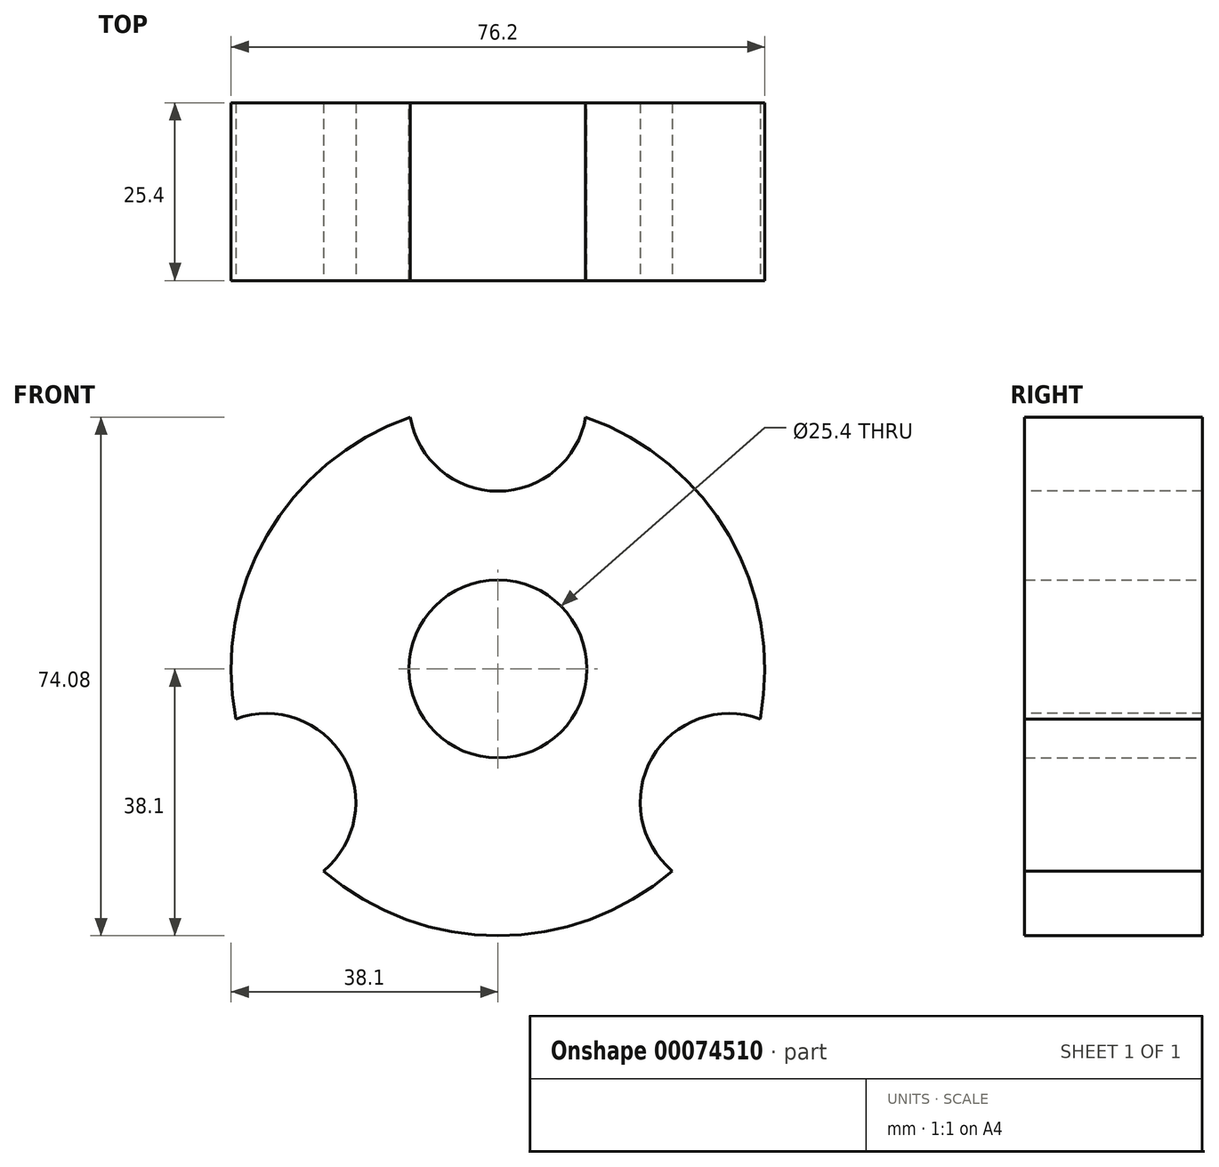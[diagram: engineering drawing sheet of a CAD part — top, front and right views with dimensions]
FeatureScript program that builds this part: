
annotation { "Feature Type Name" : "Feature", "Feature Type Description" : "" }
export const myFeature = defineFeature(function(context is Context, id is Id, definition is map)
    precondition{}
    {
        {
            var Q0;
            Q0=qCreatedBy(makeId("Front.planeOp"),FACE);
            var sketch = newSketch(context, id + "F0", { "sketchPlane" : qUnion([Q0])});
            skCircle(sketch, "E0", {"center": v(0, 0) * mm, "radius": 38.1 * mm});
            skCircle(sketch, "E1", {"center": v(0, 0) * mm, "radius": 12.7 * mm});
            skSolve(sketch);
        }
        {
            var Q0;
            Q0=makeQuery(id+"F0.imprint","IMPRINT",FACE,{"disambiguationData":[TD([[makeQuery(id+"F0.imprint","IMPRINT",EDGE,{"derivedFrom":sQuery(id+"F0.wireOp",EDGE,"E0")}),1.0]])]});
            extrude(context, id + "F1", {"entities" : qUnion([Q0]), "depth" : 25.4 * mm});
        }
        {
            var Q0;
            Q0=makeQuery(id+"F1.opExtrude","CAP_FACE",FACE,{"disambiguationData":[OSD([sQuery(id+"F0.wireOp",EDGE,"E0"),sQuery(id+"F0.wireOp",EDGE,"E1")])],"isStart":false});
            var sketch = newSketch(context, id + "F2", { "sketchPlane" : qUnion([Q0])});
            skCircle(sketch, "E2", {"center": v(0, 38.1) * mm, "radius": 12.7 * mm});
            skCircle(sketch, "E3.1.0", {"center": v(-33, -19.05) * mm, "radius": 12.7 * mm});
            skCircle(sketch, "E3.2.0", {"center": v(33, -19.05) * mm, "radius": 12.7 * mm});
            skPoint(sketch, "E3.center", {"position": v(0, 0) * mm});
            skSolve(sketch);
        }
        {
            var Q0;
            {var subQ0=sQuery(id+"F2.wireOp",EDGE,"E2");var subQ1=makeQuery(id+"F1.opExtrude","CAP_EDGE",EDGE,{"disambiguationData":[OSD([sQuery(id+"F0.wireOp",EDGE,"E0")])],"isStart":false});var subQ2=makeQuery(id+"F2.imprint","INTERSECT",VERTEX,{"disambiguationData":[OD(0.0)],"derivedFrom":[subQ1,subQ0]});Q0=makeQuery(id+"F2.imprint","IMPRINT",FACE,{"disambiguationData":[TD([[makeQuery(id+"F2.imprint","IMPRINT",EDGE,{"disambiguationData":[TD([[subQ2,1.0]])],"derivedFrom":subQ0}),1.0]])]});}
            var Q1;
            {var subQ0=sQuery(id+"F2.wireOp",EDGE,"E3.1.0");var subQ1=makeQuery(id+"F1.opExtrude","CAP_EDGE",EDGE,{"disambiguationData":[OSD([sQuery(id+"F0.wireOp",EDGE,"E0")])],"isStart":false});var subQ2=makeQuery(id+"F2.imprint","INTERSECT",VERTEX,{"disambiguationData":[OD(0.0)],"derivedFrom":[subQ1,subQ0]});Q1=makeQuery(id+"F2.imprint","IMPRINT",FACE,{"disambiguationData":[TD([[makeQuery(id+"F2.imprint","IMPRINT",EDGE,{"disambiguationData":[TD([[subQ2,-1.0]])],"derivedFrom":subQ0}),1.0]])]});}
            var Q2;
            {var subQ0=sQuery(id+"F2.wireOp",EDGE,"E3.2.0");var subQ1=makeQuery(id+"F1.opExtrude","CAP_EDGE",EDGE,{"disambiguationData":[OSD([sQuery(id+"F0.wireOp",EDGE,"E0")])],"isStart":false});var subQ2=makeQuery(id+"F2.imprint","INTERSECT",VERTEX,{"disambiguationData":[OD(0.0)],"derivedFrom":[subQ1,subQ0]});Q2=makeQuery(id+"F2.imprint","IMPRINT",FACE,{"disambiguationData":[TD([[makeQuery(id+"F2.imprint","IMPRINT",EDGE,{"disambiguationData":[TD([[subQ2,-1.0]])],"derivedFrom":subQ0}),1.0]])]});}
            var Q3;
            {var subQ0=sQuery(id+"F2.wireOp",EDGE,"E2");var subQ1=makeQuery(id+"F1.opExtrude","CAP_EDGE",EDGE,{"disambiguationData":[OSD([sQuery(id+"F0.wireOp",EDGE,"E0")])],"isStart":false});var subQ2=makeQuery(id+"F2.imprint","INTERSECT",VERTEX,{"disambiguationData":[OD(0.0)],"derivedFrom":[subQ1,subQ0]});Q3=makeQuery(id+"F2.imprint","IMPRINT",FACE,{"disambiguationData":[TD([[makeQuery(id+"F2.imprint","IMPRINT",EDGE,{"disambiguationData":[TD([[subQ2,-1.0]])],"derivedFrom":subQ0}),1.0]])]});}
            var Q4;
            {var subQ0=sQuery(id+"F2.wireOp",EDGE,"E3.2.0");var subQ1=makeQuery(id+"F1.opExtrude","CAP_EDGE",EDGE,{"disambiguationData":[OSD([sQuery(id+"F0.wireOp",EDGE,"E0")])],"isStart":false});var subQ2=makeQuery(id+"F2.imprint","INTERSECT",VERTEX,{"disambiguationData":[OD(0.0)],"derivedFrom":[subQ1,subQ0]});Q4=makeQuery(id+"F2.imprint","IMPRINT",FACE,{"disambiguationData":[TD([[makeQuery(id+"F2.imprint","IMPRINT",EDGE,{"disambiguationData":[TD([[subQ2,1.0]])],"derivedFrom":subQ0}),1.0]])]});}
            var Q5;
            {var subQ0=sQuery(id+"F2.wireOp",EDGE,"E3.1.0");var subQ1=makeQuery(id+"F1.opExtrude","CAP_EDGE",EDGE,{"disambiguationData":[OSD([sQuery(id+"F0.wireOp",EDGE,"E0")])],"isStart":false});var subQ2=makeQuery(id+"F2.imprint","INTERSECT",VERTEX,{"disambiguationData":[OD(0.0)],"derivedFrom":[subQ1,subQ0]});Q5=makeQuery(id+"F2.imprint","IMPRINT",FACE,{"disambiguationData":[TD([[makeQuery(id+"F2.imprint","IMPRINT",EDGE,{"disambiguationData":[TD([[subQ2,1.0]])],"derivedFrom":subQ0}),1.0]])]});}
            extrude(context, id + "F3", {"entities" : qUnion([Q0, Q1, Q2, Q3, Q4, Q5]), "operationType" : NewBodyOperationType.REMOVE, "oppositeDirection" : true, "depth" : 25.4 * mm});
        }
    });
